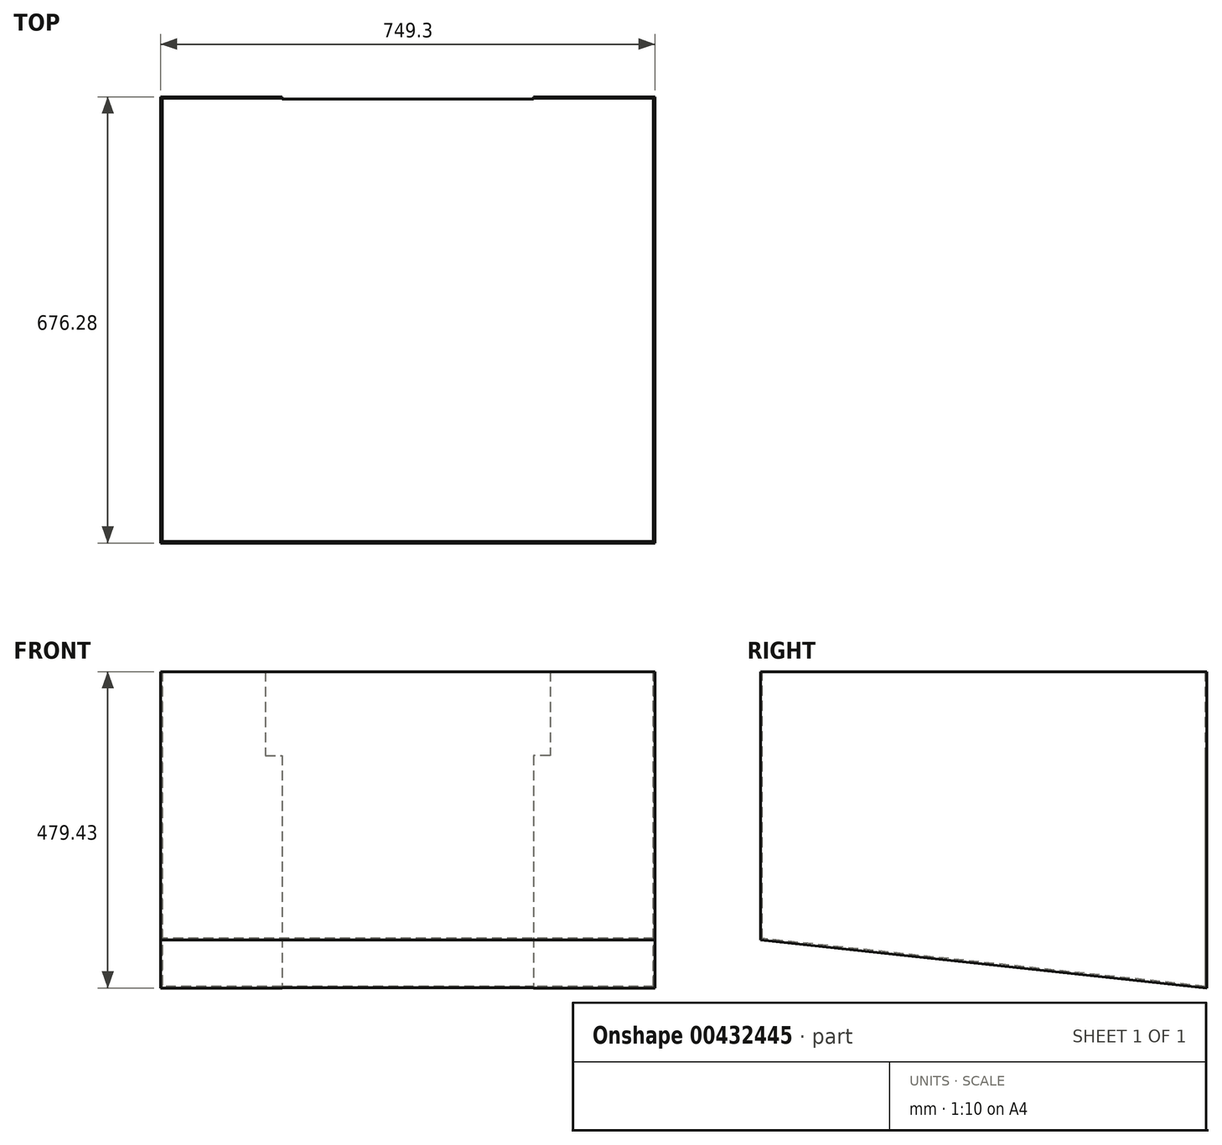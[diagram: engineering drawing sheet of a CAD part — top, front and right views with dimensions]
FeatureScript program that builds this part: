
annotation { "Feature Type Name" : "Feature", "Feature Type Description" : "" }
export const myFeature = defineFeature(function(context is Context, id is Id, definition is map)
    precondition{}
    {
        {
            var Q0;
            Q0=qCreatedBy(makeId("Right.planeOp"),FACE);
            var sketch = newSketch(context, id + "F0", { "sketchPlane" : qUnion([Q0])});
            skLineSegment(sketch, "E0", {"start": v(0, 0) * mm, "end": v(-676.28, 73.02) * mm});
            skLineSegment(sketch, "E1", {"start": v(-676.28, 73.02) * mm, "end": v(-676.28, 479.43) * mm});
            skLineSegment(sketch, "E2", {"start": v(-676.28, 479.43) * mm, "end": v(0, 479.43) * mm});
            skLineSegment(sketch, "E3", {"start": v(0, 479.43) * mm, "end": v(0, 0) * mm});
            skSolve(sketch);
        }
        {
            var Q0;
            Q0 = qSketchRegion(id + "F0", true);
            extrude(context, id + "F1", {"entities" : qUnion([Q0]), "depth" : 749.3 * mm});
        }
        {
            var Q0;
            Q0=makeQuery(id+"F1.opExtrude","SWEPT_FACE",FACE,{"disambiguationData":[OSD([sQuery(id+"F0.wireOp",EDGE,"E2")])]});
            shell(context, id + "F2", {"entities" : qUnion([Q0]), "thickness" : 2.3 * mm});
        }
        {
            var Q0;
            Q0=makeQuery(id+"F1.opExtrude","SWEPT_FACE",FACE,{"disambiguationData":[OSD([sQuery(id+"F0.wireOp",EDGE,"E3")])]});
            var sketch = newSketch(context, id + "F3", { "sketchPlane" : qUnion([Q0])});
            skLineSegment(sketch, "E4.bottom", {"start": v(-590.55, 479.43) * mm, "end": v(-158.75, 479.43) * mm});
            skLineSegment(sketch, "E4.top", {"start": v(-590.55, 0) * mm, "end": v(-158.75, 0) * mm});
            skLineSegment(sketch, "E4.left", {"start": v(-590.55, 479.43) * mm, "end": v(-590.55, 0) * mm});
            skLineSegment(sketch, "E4.right", {"start": v(-158.75, 479.43) * mm, "end": v(-158.75, 0) * mm});
            skLineSegment(sketch, "E5", {"start": v(-749.3, 239.71) * mm, "end": v(-590.55, 239.71) * mm, "construction": true});
            skLineSegment(sketch, "E6", {"start": v(-158.75, 239.71) * mm, "end": v(0, 239.71) * mm, "construction": true});
            skLineSegment(sketch, "E7.bottom", {"start": v(-158.75, 352.43) * mm, "end": v(-184.15, 352.43) * mm});
            skLineSegment(sketch, "E7.top", {"start": v(-158.75, 0) * mm, "end": v(-184.15, 0) * mm});
            skLineSegment(sketch, "E7.left", {"start": v(-158.75, 352.43) * mm, "end": v(-158.75, 0) * mm});
            skLineSegment(sketch, "E7.right", {"start": v(-184.15, 352.43) * mm, "end": v(-184.15, 0) * mm});
            skLineSegment(sketch, "E8.bottom", {"start": v(-590.55, 352.43) * mm, "end": v(-565.15, 352.43) * mm});
            skLineSegment(sketch, "E8.top", {"start": v(-590.55, 0) * mm, "end": v(-565.15, 0) * mm});
            skLineSegment(sketch, "E8.left", {"start": v(-590.55, 352.43) * mm, "end": v(-590.55, 0) * mm});
            skLineSegment(sketch, "E8.right", {"start": v(-565.15, 352.43) * mm, "end": v(-565.15, 0) * mm});
            skSolve(sketch);
        }
        {
            var Q0;
            Q0=makeQuery(id+"F3.imprint","IMPRINT",FACE,{"disambiguationData":[TD([[makeQuery(id+"F3.imprint","IMPRINT",EDGE,{"derivedFrom":sQuery(id+"F3.wireOp",EDGE,"E4.bottom")}),-1.0]])]});
            extrude(context, id + "F4", {"entities" : qUnion([Q0]), "operationType" : NewBodyOperationType.REMOVE, "oppositeDirection" : true, "depth" : 3.17 * mm});
        }
    });
